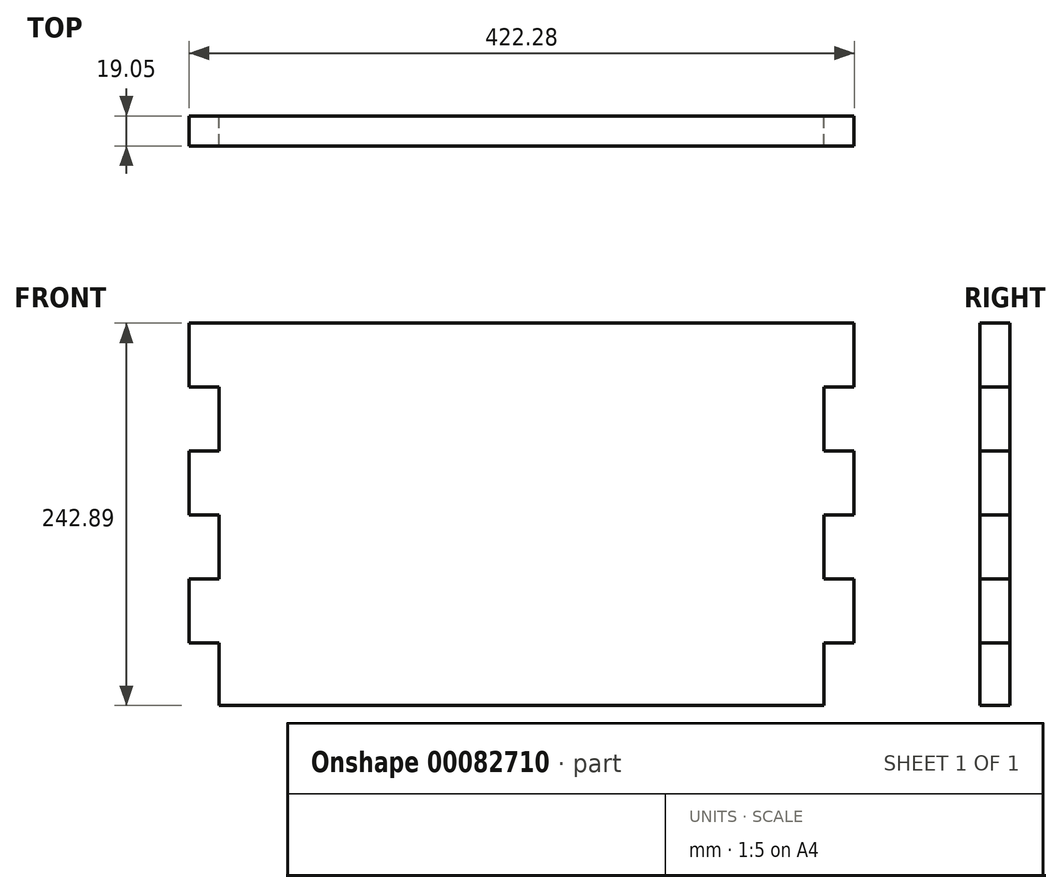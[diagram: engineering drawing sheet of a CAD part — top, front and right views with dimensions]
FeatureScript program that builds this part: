
annotation { "Feature Type Name" : "Feature", "Feature Type Description" : "" }
export const myFeature = defineFeature(function(context is Context, id is Id, definition is map)
    precondition{}
    {
        {
            var Q0;
            Q0=qCreatedBy(makeId("Front.planeOp"),FACE);
            var sketch = newSketch(context, id + "F0", { "sketchPlane" : qUnion([Q0])});
            skLineSegment(sketch, "E0.top", {"start": v(-193.16, 63.84) * mm, "end": v(-174.1, 63.84) * mm});
            skLineSegment(sketch, "E0.left", {"start": v(-193.16, 104.48) * mm, "end": v(-193.16, 63.84) * mm});
            skLineSegment(sketch, "E1.0.1.0", {"start": v(-193.16, 23.2) * mm, "end": v(-174.1, 23.2) * mm});
            skLineSegment(sketch, "E1.0.1.1", {"start": v(-174.1, 63.84) * mm, "end": v(-174.1, 23.2) * mm});
            skLineSegment(sketch, "E1.0.2.0", {"start": v(-193.16, -17.44) * mm, "end": v(-174.1, -17.44) * mm});
            skLineSegment(sketch, "E1.0.2.2", {"start": v(-193.16, 23.2) * mm, "end": v(-193.16, -17.44) * mm});
            skLineSegment(sketch, "E1.0.2.3", {"start": v(-193.16, 23.2) * mm, "end": v(-174.1, 23.2) * mm});
            skLineSegment(sketch, "E1.0.3.0", {"start": v(-193.16, -58.08) * mm, "end": v(-174.1, -58.08) * mm});
            skLineSegment(sketch, "E1.0.3.1", {"start": v(-174.1, -17.44) * mm, "end": v(-174.1, -58.08) * mm});
            skLineSegment(sketch, "E1.0.3.3", {"start": v(-193.16, -17.44) * mm, "end": v(-174.1, -17.44) * mm});
            skLineSegment(sketch, "E1.0.4.0", {"start": v(-193.16, -98.72) * mm, "end": v(-174.1, -98.72) * mm});
            skLineSegment(sketch, "E1.0.4.2", {"start": v(-193.16, -58.08) * mm, "end": v(-193.16, -98.72) * mm});
            skLineSegment(sketch, "E1.0.4.3", {"start": v(-193.16, -58.08) * mm, "end": v(-174.1, -58.08) * mm});
            skLineSegment(sketch, "E1.0.5.3", {"start": v(-193.16, -98.72) * mm, "end": v(-174.1, -98.72) * mm});
            skLineSegment(sketch, "E2", {"start": v(-174.1, -98.72) * mm, "end": v(-174.1, -138.4) * mm});
            skLineSegment(sketch, "E3.MirrorCS", {"start": v(229.12, 63.84) * mm, "end": v(210.07, 63.84) * mm});
            skLineSegment(sketch, "E4.MirrorCS", {"start": v(229.12, -58.08) * mm, "end": v(210.07, -58.08) * mm});
            skLineSegment(sketch, "E5.MirrorCS", {"start": v(229.12, 23.2) * mm, "end": v(210.07, 23.2) * mm});
            skLineSegment(sketch, "E6.MirrorCS", {"start": v(229.12, -98.72) * mm, "end": v(210.07, -98.72) * mm});
            skLineSegment(sketch, "E7.MirrorCS", {"start": v(229.12, -17.44) * mm, "end": v(210.07, -17.44) * mm});
            skLineSegment(sketch, "E8.MirrorCS", {"start": v(210.07, -98.72) * mm, "end": v(210.07, -138.4) * mm});
            skLineSegment(sketch, "E9.MirrorCS", {"start": v(229.12, -58.08) * mm, "end": v(229.12, -98.72) * mm});
            skLineSegment(sketch, "E10.MirrorCS", {"start": v(229.12, 104.48) * mm, "end": v(229.12, 63.84) * mm});
            skLineSegment(sketch, "E11.MirrorCS", {"start": v(229.12, 23.2) * mm, "end": v(229.12, -17.44) * mm});
            skLineSegment(sketch, "E12.MirrorCS", {"start": v(210.07, -17.44) * mm, "end": v(210.07, -58.08) * mm});
            skLineSegment(sketch, "E13.MirrorCS", {"start": v(210.07, 63.84) * mm, "end": v(210.07, 23.2) * mm});
            skLineSegment(sketch, "E14", {"start": v(-193.16, 104.48) * mm, "end": v(229.12, 104.48) * mm});
            skLineSegment(sketch, "E15", {"start": v(-174.1, -138.4) * mm, "end": v(210.07, -138.4) * mm});
            skSolve(sketch);
        }
        {
            var Q0;
            Q0=qSketchRegion(id+"F0",true);
            extrude(context, id + "F1", {"entities" : qUnion([Q0]), "depth" : 19.05 * mm});
        }
    });
